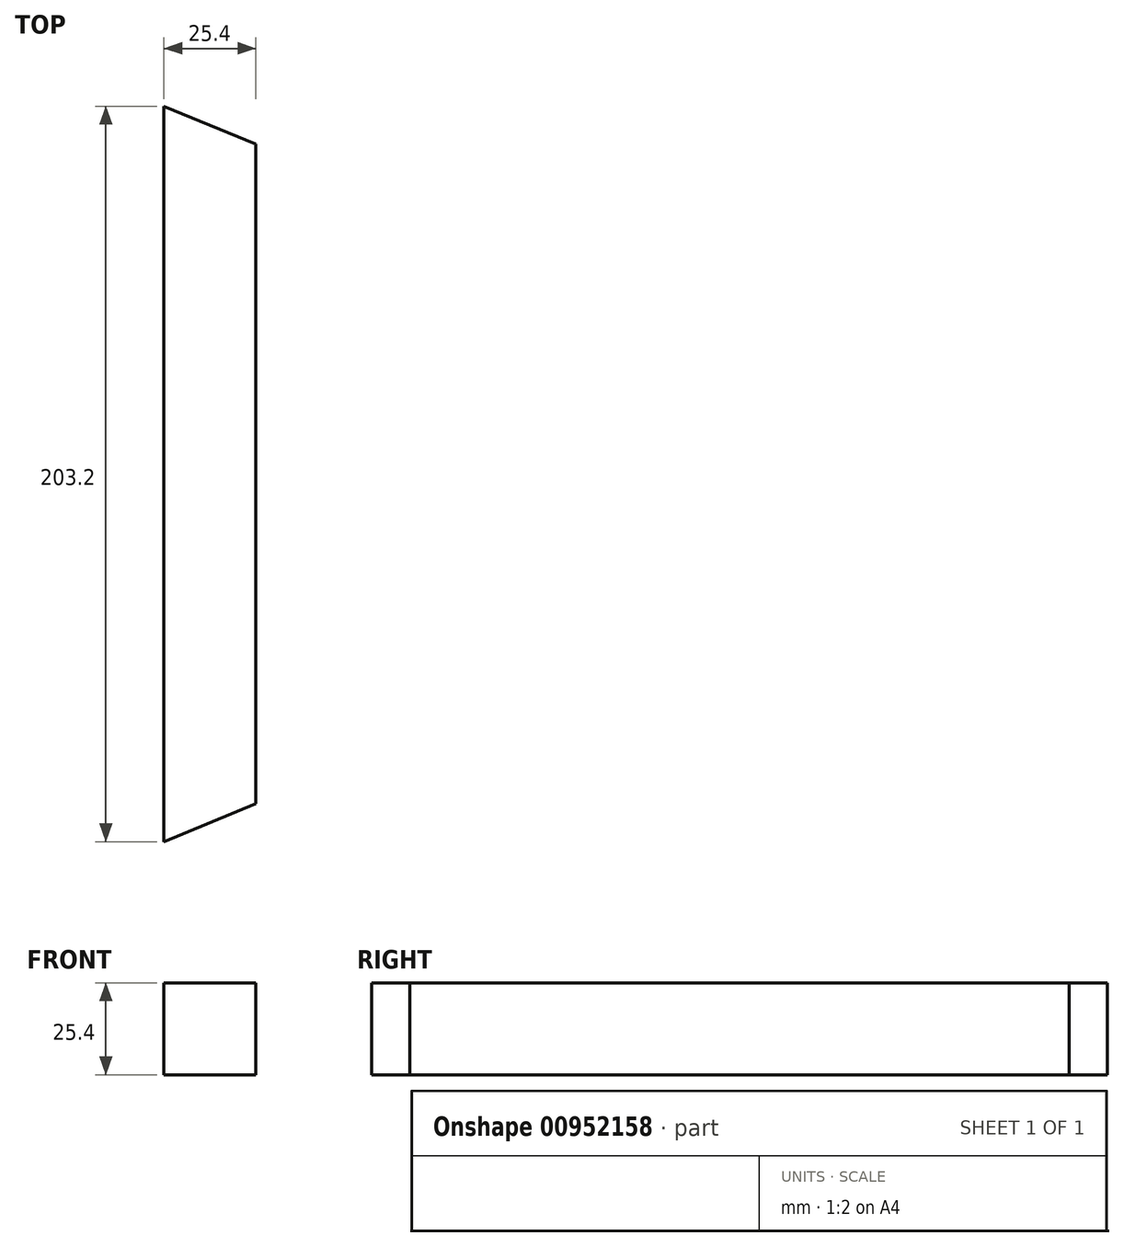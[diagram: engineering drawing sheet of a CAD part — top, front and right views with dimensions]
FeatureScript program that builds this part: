
annotation { "Feature Type Name" : "Feature", "Feature Type Description" : "" }
export const myFeature = defineFeature(function(context is Context, id is Id, definition is map)
    precondition{}
    {
        {
            var Q0;
            Q0=qCreatedBy(makeId("Front.planeOp"),FACE);
            var sketch = newSketch(context, id + "F0", { "sketchPlane" : qUnion([Q0])});
            skLineSegment(sketch, "E0.bottom", {"start": v(12.7, -12.7) * mm, "end": v(-12.7, -12.7) * mm});
            skLineSegment(sketch, "E0.top", {"start": v(12.7, 12.7) * mm, "end": v(-12.7, 12.7) * mm});
            skLineSegment(sketch, "E0.left", {"start": v(12.7, -12.7) * mm, "end": v(12.7, 12.7) * mm});
            skLineSegment(sketch, "E0.right", {"start": v(-12.7, -12.7) * mm, "end": v(-12.7, 12.7) * mm});
            skPoint(sketch, "E0.middle", {"position": v(0, 0) * mm});
            skSolve(sketch);
        }
        {
            var Q0;
            Q0 = qSketchRegion(id + "F0", true);
            extrude(context, id + "F1", {"entities" : qUnion([Q0]), "endBound" : BoundingType.SYMMETRIC, "depth" : 203.2 * mm, "offsetDistance" : 25.4 * mm});
        }
        {
            var Q0;
            Q0=makeQuery(id+"F1.opExtrude","CAP_EDGE",EDGE,{"disambiguationData":[OSD([sQuery(id+"F0.wireOp",EDGE,"E0.left")])],"isStart":false});
            var Q1;
            Q1=makeQuery(id+"F1.opExtrude","CAP_EDGE",EDGE,{"disambiguationData":[OSD([sQuery(id+"F0.wireOp",EDGE,"E0.left")])],"isStart":true});
            chamfer(context, id + "F2", {"entities" : qUnion([Q0, Q1]), "chamferType" : ChamferType.OFFSET_ANGLE, "width" : 25.4 * mm, "oppositeDirection" : false, "angle" : 22.5 * degree, "tangentPropagation" : true});
        }
    });
